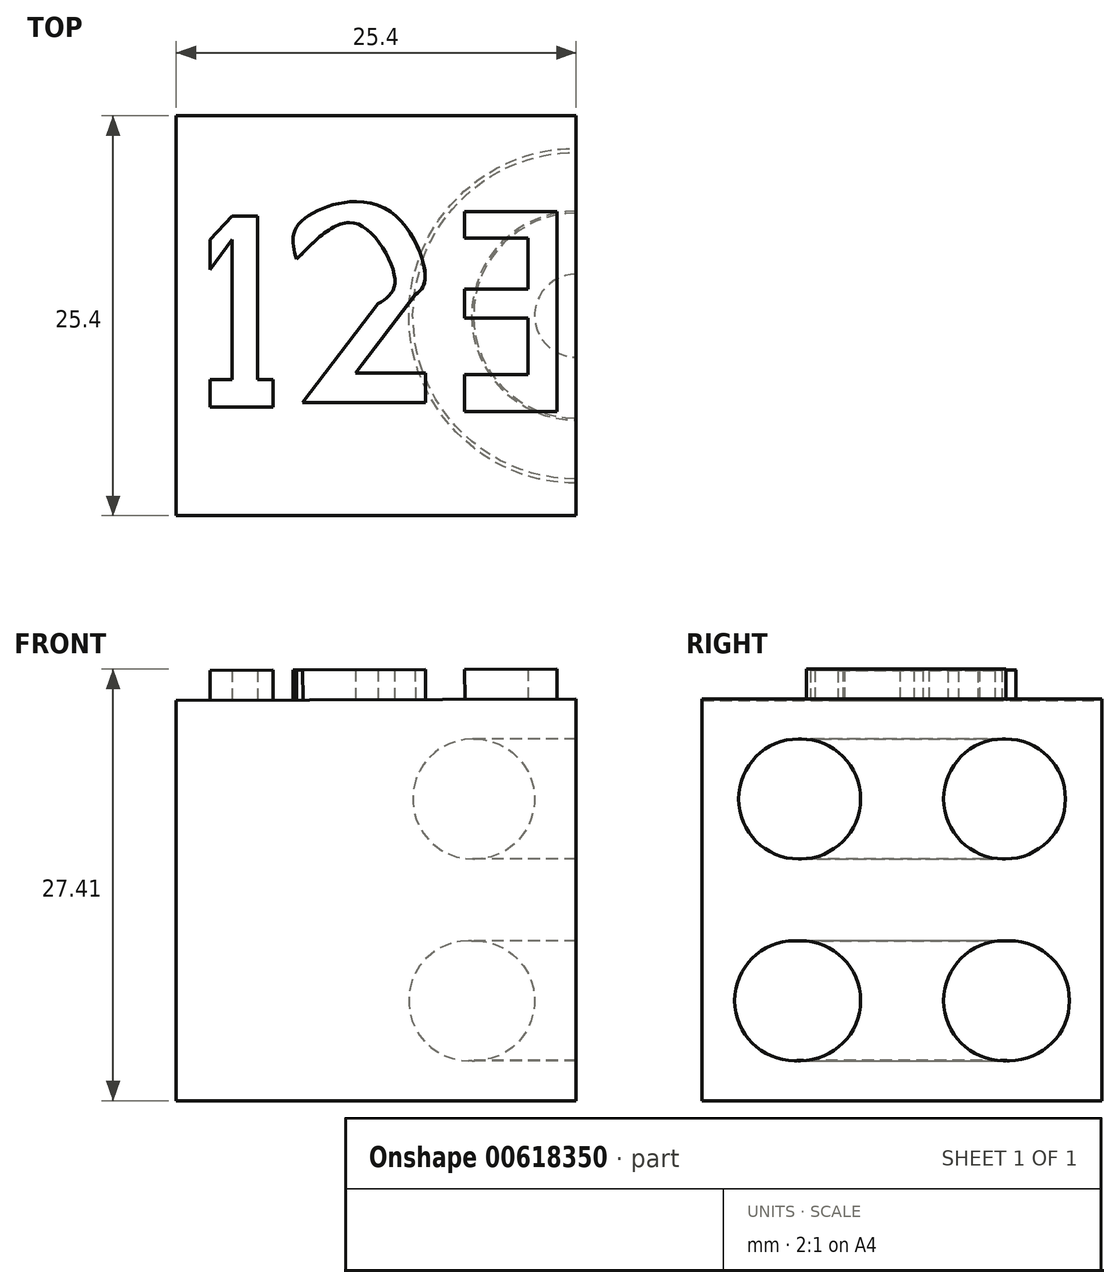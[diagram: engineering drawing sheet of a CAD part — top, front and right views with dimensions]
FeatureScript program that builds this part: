
annotation { "Feature Type Name" : "Feature", "Feature Type Description" : "" }
export const myFeature = defineFeature(function(context is Context, id is Id, definition is map)
    precondition{}
    {
        {
            var Q0;
            Q0=qCreatedBy(makeId("Front.planeOp"),FACE);
            var sketch = newSketch(context, id + "F0", { "sketchPlane" : qUnion([Q0])});
            skLineSegment(sketch, "E0", {"start": v(0, 0) * mm, "end": v(0, 25.51) * mm});
            skLineSegment(sketch, "E1", {"start": v(0, 0) * mm, "end": v(-25.4, 0) * mm});
            skLineSegment(sketch, "E2", {"start": v(-25.4, 0) * mm, "end": v(-25.4, 25.41) * mm});
            skLineSegment(sketch, "E3", {"start": v(-25.4, 25.41) * mm, "end": v(0, 25.51) * mm});
            skLineSegment(sketch, "E4", {"start": v(-25.4, 0) * mm, "end": v(0, 25.51) * mm});
            skLineSegment(sketch, "E5", {"start": v(-12.7, 0) * mm, "end": v(0, 12.76) * mm});
            skLineSegment(sketch, "E6", {"start": v(-12.7, 25.46) * mm, "end": v(-25.4, 12.7) * mm});
            skSolve(sketch);
        }
        {
            var Q0;
            Q0 = qSketchRegion(id + "F0", true);
            extrude(context, id + "F1", {"entities" : qUnion([Q0]), "depth" : 25.4 * mm, "offsetDistance" : 25.4 * mm});
        }
        {
            var Q0;
            Q0=makeQuery(id+"F1.opExtrude","CAP_FACE",FACE,{"disambiguationData":[OSD([sQuery(id+"F0.wireOp",EDGE,"E0"),sQuery(id+"F0.wireOp",EDGE,"E1"),sQuery(id+"F0.wireOp",EDGE,"E2"),sQuery(id+"F0.wireOp",EDGE,"E3")])],"isStart":false});
            var sketch = newSketch(context, id + "F2", { "sketchPlane" : qUnion([Q0])});
            skSolve(sketch);
        }
        {
            var Q0;
            Q0=sQuery(id+"F0.wireOp",EDGE,"E4");
            extrude(context, id + "F3", {"bodyType" : ToolBodyType.SURFACE, "surfaceEntities" : qUnion([Q0]), "endBound" : BoundingType.SYMMETRIC, "depth" : 2.54 * mm, "offsetDistance" : 25.4 * mm});
        }
        {
            var Q0;
            Q0=sQuery(id+"F0.wireOp",EDGE,"E5");
            extrude(context, id + "F4", {"bodyType" : ToolBodyType.SURFACE, "surfaceEntities" : qUnion([Q0]), "endBound" : BoundingType.SYMMETRIC, "depth" : 2.54 * mm, "offsetDistance" : 25.4 * mm});
        }
        {
            var Q0;
            Q0=makeQuery(id+"F1.opExtrude","SWEPT_FACE",FACE,{"disambiguationData":[OSD([sQuery(id+"F0.wireOp",EDGE,"E1")])]});
            var sketch = newSketch(context, id + "F5", { "sketchPlane" : qUnion([Q0])});
            skLineSegment(sketch, "E7", {"start": v(-19.05, 0) * mm, "end": v(-25.4, 0) * mm});
            skLineSegment(sketch, "E8", {"start": v(-19.05, 0) * mm, "end": v(-18.37, 1.1) * mm});
            skPoint(sketch, "E9.start.orphan", {"position": v(0, 0) * mm});
            skPoint(sketch, "E10.end.orphan", {"position": v(-12.7, 25.4) * mm});
            skLineSegment(sketch, "E11", {"start": v(-25.4, 0) * mm, "end": v(-12.7, 25.4) * mm});
            skLineSegment(sketch, "E12", {"start": v(-12.7, 25.4) * mm, "end": v(0, 0) * mm});
            skLineSegment(sketch, "E13", {"start": v(-25.4, 0) * mm, "end": v(0, 0) * mm});
            skLineSegment(sketch, "E14", {"start": v(-19.05, 25.4) * mm, "end": v(-25.4, 12.7) * mm});
            skLineSegment(sketch, "E15", {"start": v(0, 12.7) * mm, "end": v(-6.35, 25.4) * mm});
            skLineSegment(sketch, "E16", {"start": v(-12.7, 15.09) * mm, "end": v(-18.37, 3.75) * mm});
            skPoint(sketch, "E16.startSnap0", {"position": v(-12.7, 0) * mm});
            skLineSegment(sketch, "E17", {"start": v(-18.37, 3.75) * mm, "end": v(-6.35, 3.75) * mm});
            skLineSegment(sketch, "E18", {"start": v(-6.35, 3.75) * mm, "end": v(-12.7, 15.09) * mm});
            skSolve(sketch);
        }
        {
            var Q0;
            Q0=makeQuery(id+"F2.imprint","IMPRINT",FACE,{"disambiguationData":[TD([[makeQuery(id+"F2.imprint","IMPRINT",EDGE,{"derivedFrom":makeQuery(id+"F1.opExtrude","CAP_EDGE",EDGE,{"disambiguationData":[OSD([sQuery(id+"F0.wireOp",EDGE,"E0")])],"isStart":false})}),1.0]])]});
            var sketch = newSketch(context, id + "F6", { "sketchPlane" : qUnion([Q0])});
            skLineSegment(sketch, "E19", {"start": v(0, 0) * mm, "end": v(0, 25.4) * mm});
            skLineSegment(sketch, "E20", {"start": v(0, 25.4) * mm, "end": v(-25.4, 25.4) * mm});
            skLineSegment(sketch, "E21", {"start": v(-25.4, 25.4) * mm, "end": v(-25.4, 0) * mm});
            skCircle(sketch, "E22", {"center": v(-12.7, 12.7) * mm, "radius": 11.35 * mm});
            skCircle(sketch, "E23", {"center": v(-12.7, 12.7) * mm, "radius": 8.87 * mm});
            skCircle(sketch, "E24", {"center": v(-12.7, 12.7) * mm, "radius": 5.52 * mm});
            skCircle(sketch, "E25", {"center": v(-12.7, 12.7) * mm, "radius": 3 * mm});
            skCircle(sketch, "E26", {"center": v(-12.7, 25.4) * mm, "radius": 1.35 * mm});
            skCircle(sketch, "E27", {"center": v(-12.7, 12.7) * mm, "radius": 12.47 * mm});
            skSolve(sketch);
        }
        {
            var Q0;
            Q0=sQuery(id+"F6.wireOp",EDGE,"E22");
            var Q1;
            Q1=sQuery(id+"F6.wireOp",EDGE,"E25");
            var Q2;
            Q2=sQuery(id+"F6.wireOp",EDGE,"E24");
            var Q3;
            Q3=sQuery(id+"F6.wireOp",EDGE,"E23");
            extrude(context, id + "F7", {"bodyType" : ToolBodyType.SURFACE, "surfaceEntities" : qUnion([Q0, Q1, Q2, Q3]), "endBound" : BoundingType.SYMMETRIC, "oppositeDirection" : true, "depth" : 1.27 * mm, "offsetDistance" : 25.4 * mm});
        }
        {
            var Q0;
            Q0=sQuery(id+"F0.wireOp",EDGE,"E6");
            extrude(context, id + "F8", {"bodyType" : ToolBodyType.SURFACE, "surfaceEntities" : qUnion([Q0]), "endBound" : BoundingType.SYMMETRIC, "depth" : 2.54 * mm, "offsetDistance" : 25.4 * mm});
        }
        {
            var Q0;
            Q0=sQuery(id+"F6.wireOp",EDGE,"E22");
            var Q1;
            Q1=sQuery(id+"F6.wireOp",EDGE,"E23");
            var Q2;
            Q2=sQuery(id+"F6.wireOp",EDGE,"E24");
            var Q3;
            Q3=sQuery(id+"F6.wireOp",EDGE,"E25");
            extrude(context, id + "F9", {"bodyType" : ToolBodyType.SURFACE, "surfaceEntities" : qUnion([Q0, Q1, Q2, Q3]), "depth" : 1.27 * mm, "offsetDistance" : 25.4 * mm});
        }
        {
            var Q0;
            Q0=sQuery(id+"F6.wireOp",EDGE,"E22");
            var Q1;
            Q1=sQuery(id+"F6.wireOp",EDGE,"E23");
            var Q2;
            Q2=sQuery(id+"F6.wireOp",EDGE,"E24");
            var Q3;
            Q3=sQuery(id+"F6.wireOp",EDGE,"E25");
            extrude(context, id + "F10", {"bodyType" : ToolBodyType.SURFACE, "surfaceEntities" : qUnion([Q0, Q1, Q2, Q3]), "depth" : 1.27 * mm, "offsetDistance" : 25.4 * mm});
        }
        {
            var Q0;
            Q0=sQuery(id+"F5.wireOp",EDGE,"E14");
            var Q1;
            Q1=sQuery(id+"F5.wireOp",EDGE,"E11");
            var Q2;
            Q2=sQuery(id+"F5.wireOp",EDGE,"E16");
            var Q3;
            Q3=sQuery(id+"F5.wireOp",EDGE,"E17");
            var Q4;
            Q4=sQuery(id+"F5.wireOp",EDGE,"E18");
            var Q5;
            Q5=sQuery(id+"F5.wireOp",EDGE,"E12");
            var Q6;
            Q6=sQuery(id+"F5.wireOp",EDGE,"E15");
            var Q7;
            Q7=sQuery(id+"F5.wireOp",EDGE,"E13");
            extrude(context, id + "F11", {"bodyType" : ToolBodyType.SURFACE, "surfaceEntities" : qUnion([Q0, Q1, Q2, Q3, Q4, Q5, Q6, Q7]), "depth" : 1.27 * mm, "offsetDistance" : 25.4 * mm});
        }
        {
            var Q0;
            Q0=makeQuery(id+"F1.opExtrude","SWEPT_FACE",FACE,{"disambiguationData":[OSD([sQuery(id+"F0.wireOp",EDGE,"E0")])]});
            var sketch = newSketch(context, id + "F12", { "sketchPlane" : qUnion([Q0])});
            skPoint(sketch, "E28.startSnap0", {"position": v(-25.4, 12.76) * mm});
            skLineSegment(sketch, "E29", {"start": v(-12.7, 25.51) * mm, "end": v(-12.7, 0) * mm});
            skLineSegment(sketch, "E30", {"start": v(-25.4, 12.76) * mm, "end": v(0, 12.76) * mm});
            skCircle(sketch, "E31", {"center": v(-19.27, 19.16) * mm, "radius": 3.81 * mm});
            skCircle(sketch, "E32", {"center": v(-6.25, 6.35) * mm, "radius": 3.81 * mm});
            skCircle(sketch, "E33", {"center": v(-19.52, 6.35) * mm, "radius": 3.81 * mm});
            skCircle(sketch, "E34", {"center": v(-6.25, 19.16) * mm, "radius": 3.81 * mm});
            skSolve(sketch);
        }
        {
            var Q0;
            Q0=makeQuery(id+"F12.imprint","IMPRINT",FACE,{"disambiguationData":[TD([[makeQuery(id+"F12.imprint","IMPRINT",EDGE,{"derivedFrom":sQuery(id+"F12.wireOp",EDGE,"E31")}),1.0]])]});
            var Q1;
            Q1=makeQuery(id+"F12.imprint","IMPRINT",FACE,{"disambiguationData":[TD([[makeQuery(id+"F12.imprint","IMPRINT",EDGE,{"derivedFrom":sQuery(id+"F12.wireOp",EDGE,"E34")}),1.0]])]});
            var Q2;
            Q2=makeQuery(id+"F12.imprint","IMPRINT",FACE,{"disambiguationData":[TD([[makeQuery(id+"F12.imprint","IMPRINT",EDGE,{"derivedFrom":sQuery(id+"F12.wireOp",EDGE,"E32")}),1.0]])]});
            var Q3;
            Q3=makeQuery(id+"F12.imprint","IMPRINT",FACE,{"disambiguationData":[TD([[makeQuery(id+"F12.imprint","IMPRINT",EDGE,{"derivedFrom":sQuery(id+"F12.wireOp",EDGE,"E33")}),1.0]])]});
            var Q4;
            Q4=sQuery(id+"F12.wireOp",EDGE,"E29");
            revolve(context, id + "F13", {"operationType" : NewBodyOperationType.REMOVE, "entities" : qUnion([Q0, Q1, Q2, Q3]), "axis" : qUnion([Q4]), "revolveType" : RevolveType.FULL});
        }
        {
            var Q0;
            Q0=makeQuery(id+"F1.opExtrude","SWEPT_FACE",FACE,{"disambiguationData":[OSD([sQuery(id+"F0.wireOp",EDGE,"E2")])]});
            var sketch = newSketch(context, id + "F14", { "sketchPlane" : qUnion([Q0])});
            skLineSegment(sketch, "E35", {"start": v(0, 12.7) * mm, "end": v(12.7, 0) * mm});
            skLineSegment(sketch, "E36", {"start": v(12.7, 0) * mm, "end": v(25.4, 12.7) * mm});
            skLineSegment(sketch, "E37", {"start": v(25.4, 12.7) * mm, "end": v(12.69, 25.41) * mm});
            skLineSegment(sketch, "E38", {"start": v(12.69, 25.41) * mm, "end": v(0, 12.7) * mm});
            skLineSegment(sketch, "E39", {"start": v(6.34, 19.06) * mm, "end": v(6.34, 6.36) * mm});
            skLineSegment(sketch, "E40", {"start": v(6.34, 6.36) * mm, "end": v(19.06, 6.36) * mm});
            skLineSegment(sketch, "E41", {"start": v(19.06, 6.36) * mm, "end": v(19.06, 19.04) * mm});
            skLineSegment(sketch, "E42", {"start": v(19.06, 19.04) * mm, "end": v(6.34, 19.06) * mm});
            skLineSegment(sketch, "E43", {"start": v(6.34, 12.7) * mm, "end": v(12.68, 6.36) * mm});
            skPoint(sketch, "E43.startSnap0", {"position": v(19.06, 12.7) * mm});
            skLineSegment(sketch, "E44", {"start": v(12.68, 6.36) * mm, "end": v(19.06, 12.7) * mm});
            skLineSegment(sketch, "E45", {"start": v(12.7, 19.05) * mm, "end": v(6.34, 12.7) * mm});
            skLineSegment(sketch, "E46", {"start": v(12.7, 19.05) * mm, "end": v(19.06, 12.7) * mm});
            skLineSegment(sketch, "E47", {"start": v(9.51, 15.86) * mm, "end": v(9.5, 9.54) * mm});
            skPoint(sketch, "E47.startSnap0", {"position": v(9.51, 9.53) * mm});
            skLineSegment(sketch, "E48", {"start": v(9.5, 9.54) * mm, "end": v(15.83, 9.53) * mm});
            skLineSegment(sketch, "E49", {"start": v(15.83, 9.53) * mm, "end": v(15.83, 15.93) * mm});
            skLineSegment(sketch, "E50", {"start": v(15.83, 15.93) * mm, "end": v(9.51, 15.86) * mm});
            skSolve(sketch);
        }
        {
            var Q0;
            Q0=makeQuery(id+"F1.opExtrude","SWEPT_FACE",FACE,{"disambiguationData":[OSD([sQuery(id+"F0.wireOp",EDGE,"E3")])]});
            var sketch = newSketch(context, id + "F15", { "sketchPlane" : qUnion([Q0])});
            skLineSegment(sketch, "E51", {"start": v(-21.73, -7.87) * mm, "end": v(-23.13, -9.78) * mm});
            skLineSegment(sketch, "E52", {"start": v(-23.13, -9.78) * mm, "end": v(-21.73, -7.87) * mm});
            skLineSegment(sketch, "E53", {"start": v(-23.13, -18.51) * mm, "end": v(-19.14, -18.51) * mm});
            skLineSegment(sketch, "E54", {"start": v(-19.14, -18.51) * mm, "end": v(-19.14, -16.77) * mm});
            skLineSegment(sketch, "E55", {"start": v(-19.14, -16.77) * mm, "end": v(-20.13, -16.77) * mm});
            skLineSegment(sketch, "E56", {"start": v(-20.13, -16.77) * mm, "end": v(-20.13, -7.87) * mm});
            skLineSegment(sketch, "E57", {"start": v(-20.13, -7.87) * mm, "end": v(-20.13, -6.37) * mm});
            skLineSegment(sketch, "E58", {"start": v(-20.13, -6.37) * mm, "end": v(-21.73, -6.37) * mm});
            skLineSegment(sketch, "E59", {"start": v(-21.73, -6.37) * mm, "end": v(-23.13, -7.87) * mm});
            skLineSegment(sketch, "E60", {"start": v(-23.13, -7.87) * mm, "end": v(-23.13, -9.78) * mm});
            skLineSegment(sketch, "E61", {"start": v(-21.3, -16.77) * mm, "end": v(-23.13, -16.77) * mm});
            skLineSegment(sketch, "E62", {"start": v(-23.13, -16.77) * mm, "end": v(-23.13, -18.51) * mm});
            skLineSegment(sketch, "E63", {"start": v(-9.45, -18.22) * mm, "end": v(-17.25, -18.22) * mm});
            skLineSegment(sketch, "E64", {"start": v(-17.25, -18.22) * mm, "end": v(-12.48, -11.94) * mm});
            skFitSpline(sketch, "E65", {"points": [v(-12.48, -11.94) * mm, v(-11.4, -10.6) * mm, v(-13.81, -6.86) * mm, v(-17.64, -9.11) * mm], "startDerivative": vector(6.63, 3.93) * mm, "endDerivative": vector(-10.14, -10.5) * mm});
            skFitSpline(sketch, "E66", {"points": [v(-9.45, -18.22) * mm, v(-9.45, -16.35) * mm], "startDerivative": vector(0, 1.83) * mm, "endDerivative": vector(0, 1.83) * mm});
            skLineSegment(sketch, "E67", {"start": v(-9.45, -16.35) * mm, "end": v(-13.9, -16.35) * mm});
            skLineSegment(sketch, "E68", {"start": v(-13.9, -16.35) * mm, "end": v(-10.1, -11.37) * mm});
            skFitSpline(sketch, "E69", {"points": [v(-10.1, -11.37) * mm, v(-9.48, -10.36) * mm, v(-12.23, -5.78) * mm, v(-17.56, -6.95) * mm, v(-17.64, -9.11) * mm], "startDerivative": vector(5.75, 4.58) * mm, "endDerivative": vector(3.18, -10.88) * mm});
            skLineSegment(sketch, "E70", {"start": v(-6.96, -6.1) * mm, "end": v(-1.1, -6.1) * mm});
            skLineSegment(sketch, "E71", {"start": v(-1.1, -6.1) * mm, "end": v(-1.1, -12.12) * mm});
            skLineSegment(sketch, "E72", {"start": v(-1.1, -12.12) * mm, "end": v(-1.1, -18.78) * mm});
            skLineSegment(sketch, "E73", {"start": v(-1.1, -18.78) * mm, "end": v(-6.96, -18.78) * mm});
            skLineSegment(sketch, "E74", {"start": v(-6.96, -18.78) * mm, "end": v(-6.96, -16.46) * mm});
            skLineSegment(sketch, "E75", {"start": v(-6.96, -16.46) * mm, "end": v(-2.95, -16.46) * mm});
            skLineSegment(sketch, "E76", {"start": v(-2.95, -16.46) * mm, "end": v(-2.95, -12.84) * mm});
            skLineSegment(sketch, "E77", {"start": v(-2.95, -12.84) * mm, "end": v(-6.96, -12.84) * mm});
            skLineSegment(sketch, "E78", {"start": v(-6.96, -12.84) * mm, "end": v(-6.96, -11) * mm});
            skLineSegment(sketch, "E79", {"start": v(-6.96, -6.1) * mm, "end": v(-6.96, -7.79) * mm});
            skLineSegment(sketch, "E80", {"start": v(-6.96, -7.79) * mm, "end": v(-2.95, -7.79) * mm});
            skLineSegment(sketch, "E81", {"start": v(-2.95, -7.79) * mm, "end": v(-2.95, -11) * mm});
            skLineSegment(sketch, "E82", {"start": v(-2.95, -11) * mm, "end": v(-6.96, -11) * mm});
            skLineSegment(sketch, "E83", {"start": v(-21.73, -7.87) * mm, "end": v(-21.73, -16.77) * mm});
            skSolve(sketch);
        }
        {
            var Q0;
            Q0=sQuery(id+"F14.wireOp",EDGE,"E36");
            var Q1;
            Q1=sQuery(id+"F14.wireOp",EDGE,"E35");
            var Q2;
            Q2=sQuery(id+"F14.wireOp",EDGE,"E38");
            var Q3;
            Q3=sQuery(id+"F14.wireOp",EDGE,"E37");
            var Q4;
            Q4=sQuery(id+"F14.wireOp",EDGE,"E46");
            var Q5;
            Q5=sQuery(id+"F14.wireOp",EDGE,"E44");
            var Q6;
            Q6=sQuery(id+"F14.wireOp",EDGE,"E43");
            var Q7;
            Q7=sQuery(id+"F14.wireOp",EDGE,"E45");
            extrude(context, id + "F16", {"bodyType" : ToolBodyType.SURFACE, "surfaceEntities" : qUnion([Q0, Q1, Q2, Q3, Q4, Q5, Q6, Q7]), "endBound" : BoundingType.SYMMETRIC, "depth" : 2.54 * mm, "offsetDistance" : 25.4 * mm});
        }
        {
            var Q0;
            Q0 = qSketchRegion(id + "F15", true);
            extrude(context, id + "F17", {"entities" : qUnion([Q0]), "operationType" : NewBodyOperationType.ADD, "depth" : 1.9 * mm, "offsetDistance" : 25.4 * mm});
        }
    });
